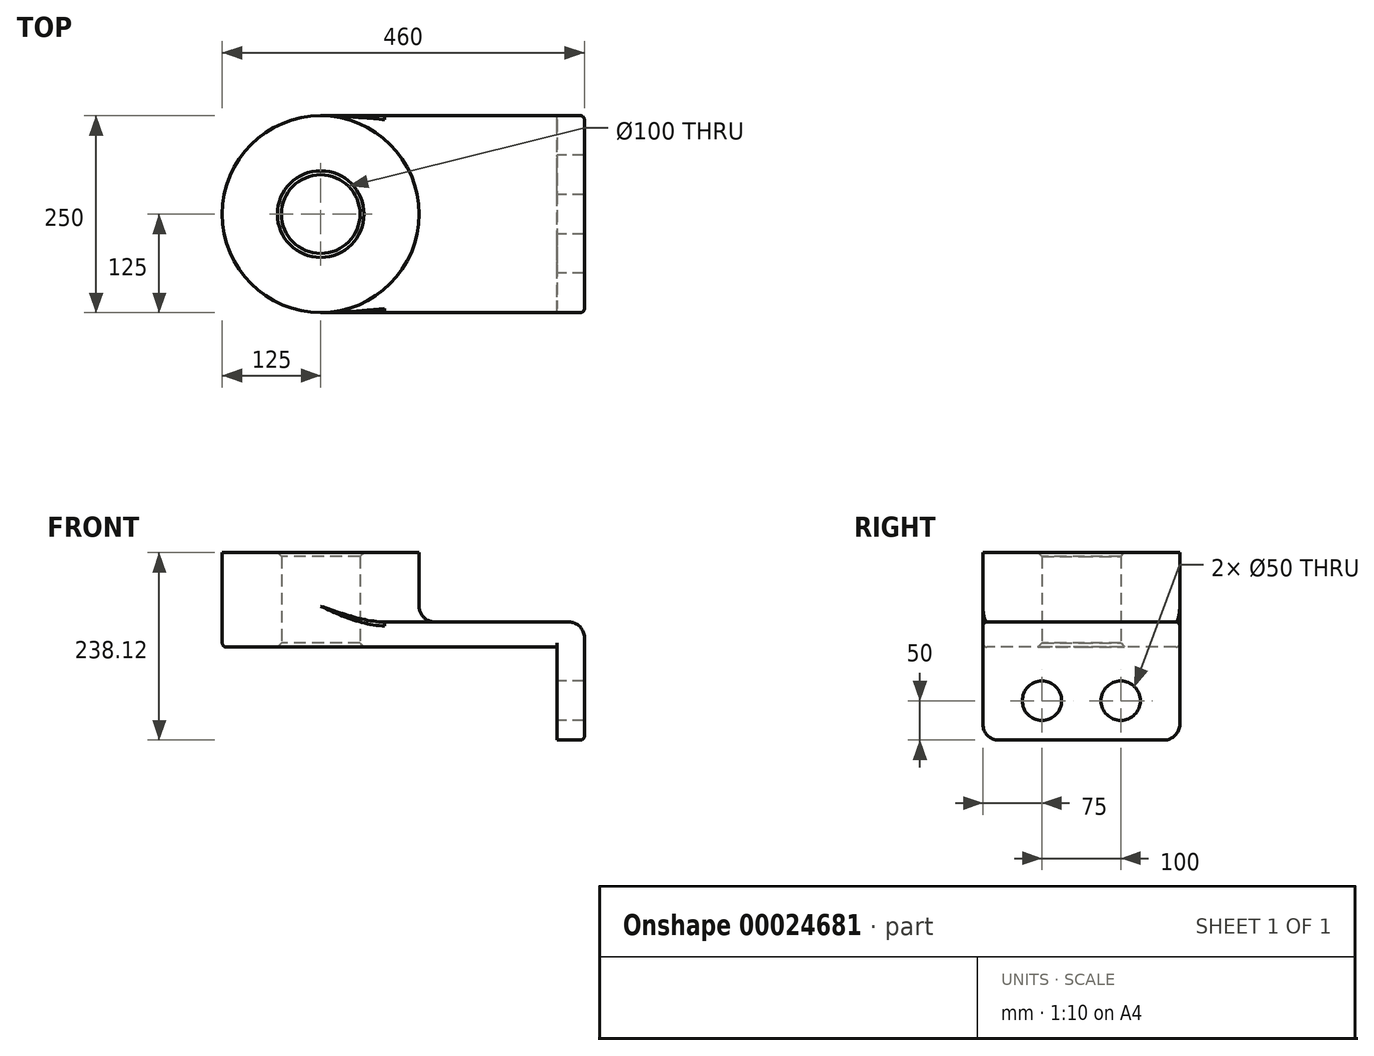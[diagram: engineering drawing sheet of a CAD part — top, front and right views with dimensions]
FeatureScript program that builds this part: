
annotation { "Feature Type Name" : "Feature", "Feature Type Description" : "" }
export const myFeature = defineFeature(function(context is Context, id is Id, definition is map)
    precondition{}
    {
        {
            var Q0;
            Q0=qCreatedBy(makeId("Top.planeOp"),FACE);
            var sketch = newSketch(context, id + "F0", { "sketchPlane" : qUnion([Q0])});
            skLineSegment(sketch, "E0.rect.bottom", {"start": v(-150, 125) * mm, "end": v(150, 125) * mm});
            skLineSegment(sketch, "E0.rect.top", {"start": v(-150, -125) * mm, "end": v(150, -125) * mm});
            skLineSegment(sketch, "E0.rect.left", {"start": v(-150, 125) * mm, "end": v(-150, -125) * mm});
            skLineSegment(sketch, "E0.rect.right", {"start": v(150, 125) * mm, "end": v(150, -125) * mm});
            skPoint(sketch, "E0.rect.middle", {"position": v(0, 0) * mm});
            skCircle(sketch, "E1", {"center": v(-150, 0) * mm, "radius": 125 * mm});
            skCircle(sketch, "E2", {"center": v(-150, 0) * mm, "radius": 50 * mm});
            skSolve(sketch);
        }
        {
            var Q0;
            Q0 = qSketchRegion(id + "F0", true);
            extrude(context, id + "F1", {"entities" : qUnion([Q0]), "depth" : 31.88 * mm});
        }
        {
            var Q0;
            {var subQ0=sQuery(id+"F0.wireOp",EDGE,"E2");var subQ1=sQuery(id+"F0.wireOp",EDGE,"E0.rect.left");var subQ3=makeQuery(id+"F0.imprint","INTERSECT",VERTEX,{"disambiguationData":[OD(0.0)],"derivedFrom":[subQ1,subQ0]});Q0=makeQuery(id+"F0.imprint","IMPRINT",FACE,{"disambiguationData":[TD([[makeQuery(id+"F0.imprint","IMPRINT",EDGE,{"disambiguationData":[TD([[subQ3,-1.0]])],"derivedFrom":subQ0}),-1.0]])]});}
            var Q1;
            {var subQ0=sQuery(id+"F0.wireOp",EDGE,"E2");var subQ1=sQuery(id+"F0.wireOp",EDGE,"E0.rect.left");var subQ3=makeQuery(id+"F0.imprint","INTERSECT",VERTEX,{"disambiguationData":[OD(0.0)],"derivedFrom":[subQ1,subQ0]});Q1=makeQuery(id+"F0.imprint","IMPRINT",FACE,{"disambiguationData":[TD([[makeQuery(id+"F0.imprint","IMPRINT",EDGE,{"disambiguationData":[TD([[subQ3,1.0]])],"derivedFrom":subQ0}),-1.0]])]});}
            extrude(context, id + "F2", {"entities" : qUnion([Q0, Q1]), "operationType" : NewBodyOperationType.ADD, "depth" : 120 * mm});
        }
        {
            var Q0;
            Q0=makeQuery(id+"F1.opExtrude","SWEPT_FACE",FACE,{"disambiguationData":[OSD([sQuery(id+"F0.wireOp",EDGE,"E0.rect.right")])]});
            var sketch = newSketch(context, id + "F3", { "sketchPlane" : qUnion([Q0])});
            skLineSegment(sketch, "E3.bottom", {"start": v(-125, 31.88) * mm, "end": v(125, 31.88) * mm});
            skLineSegment(sketch, "E3.top", {"start": v(-125, -118.12) * mm, "end": v(125, -118.12) * mm});
            skLineSegment(sketch, "E3.left", {"start": v(-125, 31.88) * mm, "end": v(-125, -118.12) * mm});
            skLineSegment(sketch, "E3.right", {"start": v(125, 31.88) * mm, "end": v(125, -118.12) * mm});
            skCircle(sketch, "E4", {"center": v(-50, -68.12) * mm, "radius": 25 * mm});
            skLineSegment(sketch, "E5", {"start": v(0, 0) * mm, "end": v(0, -118.12) * mm, "construction": true});
            skCircle(sketch, "E6.MirrorC", {"center": v(50, -68.12) * mm, "radius": 25 * mm});
            skSolve(sketch);
        }
        {
            var Q0;
            Q0 = qSketchRegion(id + "F3", true);
            extrude(context, id + "F4", {"entities" : qUnion([Q0]), "operationType" : NewBodyOperationType.ADD, "depth" : 35 * mm});
        }
        {
            var Q0;
            {var subQ0=sQuery(id+"F0.wireOp",EDGE,"E1");Q0=makeQuery(id+"F2.boolean.opBoolean","INTERSECT",EDGE,{"derivedFrom":[makeQuery(id+"F1.opExtrude","CAP_FACE",FACE,{"disambiguationData":[OSD([sQuery(id+"F0.wireOp",EDGE,"E0.rect.bottom"),sQuery(id+"F0.wireOp",EDGE,"E0.rect.top"),sQuery(id+"F0.wireOp",EDGE,"E0.rect.right"),subQ0,sQuery(id+"F0.wireOp",EDGE,"E2")])],"isStart":false}),makeQuery(id+"F2.opExtrude","SWEPT_FACE",FACE,{"disambiguationData":[OSD([subQ0])]})]});}
            var Q1;
            Q1=makeQuery(id+"F4.opExtrude","CAP_EDGE",EDGE,{"disambiguationData":[OSD([sQuery(id+"F3.wireOp",EDGE,"E3.bottom")])],"isStart":false});
            var Q2;
            Q2=makeQuery(id+"F4.opExtrude","SWEPT_EDGE",EDGE,{"disambiguationData":[OSD([sQuery(id+"F3.wireOp",EDGE,"E3.top"),sQuery(id+"F3.wireOp",EDGE,"E3.left")])]});
            var Q3;
            Q3=makeQuery(id+"F4.opExtrude","SWEPT_EDGE",EDGE,{"disambiguationData":[OSD([sQuery(id+"F3.wireOp",EDGE,"E3.top"),sQuery(id+"F3.wireOp",EDGE,"E3.right")])]});
            fillet(context, id + "F5", {"entities" : qUnion([Q0, Q1, Q2, Q3]), "radius" : 20 * mm, "tangentPropagation" : true, "allowEdgeOverflow" : false});
        }
        {
            var Q0;
            Q0=makeQuery(id+"F1.opExtrude","CAP_EDGE",EDGE,{"disambiguationData":[OSD([sQuery(id+"F0.wireOp",EDGE,"E0.rect.top")])],"isStart":true});
            var Q1;
            Q1=makeQuery(id+"F1.opExtrude","CAP_EDGE",EDGE,{"disambiguationData":[OSD([sQuery(id+"F0.wireOp",EDGE,"E0.rect.right")])],"isStart":true});
            var Q2;
            Q2=makeQuery(id+"F4.boolean.opBoolean","MERGE",EDGE,{"derivedFrom":[makeQuery(id+"F1.opExtrude","CAP_EDGE",EDGE,{"disambiguationData":[OSD([sQuery(id+"F0.wireOp",EDGE,"E0.rect.top")])],"isStart":false}),makeQuery(id+"F4.opExtrude","SWEPT_EDGE",EDGE,{"disambiguationData":[OSD([sQuery(id+"F3.wireOp",EDGE,"E3.bottom"),sQuery(id+"F3.wireOp",EDGE,"E3.left")])]})]});
            fillet(context, id + "F6", {"entities" : qUnion([Q0, Q1, Q2]), "radius" : 5 * mm, "tangentPropagation" : true, "allowEdgeOverflow" : false});
        }
        {
            var Q0;
            {var subQ0=sQuery(id+"F0.wireOp",EDGE,"E2");Q0=makeQuery(id+"F2.boolean.opBoolean","MERGE",FACE,{"derivedFrom":[makeQuery(id+"F1.opExtrude","SWEPT_FACE",FACE,{"disambiguationData":[OSD([subQ0])]}),makeQuery(id+"F2.opExtrude","SWEPT_FACE",FACE,{"disambiguationData":[OSD([subQ0])]})]});}
            chamfer(context, id + "F7", {"entities" : qUnion([Q0]), "width" : 5 * mm, "tangentPropagation" : true});
        }
    });
